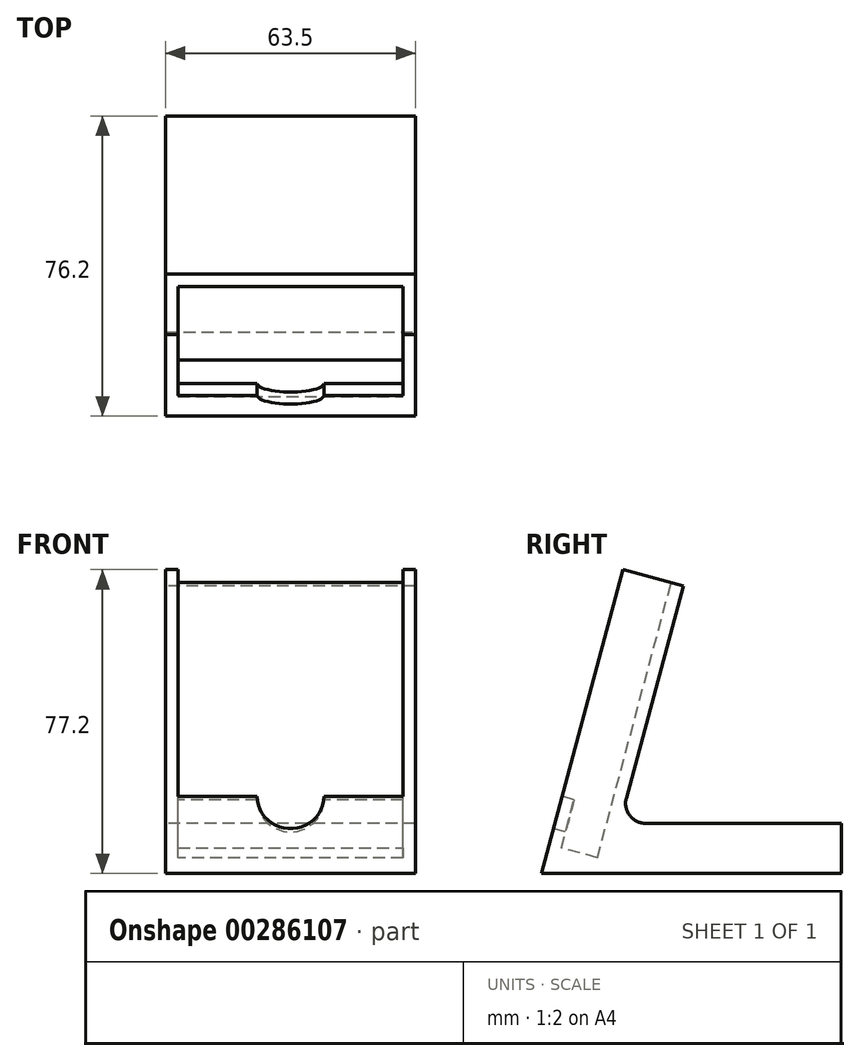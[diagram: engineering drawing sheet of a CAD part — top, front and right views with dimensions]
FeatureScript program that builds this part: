
annotation { "Feature Type Name" : "Feature", "Feature Type Description" : "" }
export const myFeature = defineFeature(function(context is Context, id is Id, definition is map)
    precondition{}
    {
        {
            var Q0;
            Q0=qCreatedBy(makeId("Right.planeOp"),FACE);
            var sketch = newSketch(context, id + "F0", { "sketchPlane" : qUnion([Q0])});
            skLineSegment(sketch, "E0", {"start": v(0, 0) * mm, "end": v(76.2, 0) * mm});
            skLineSegment(sketch, "E1", {"start": v(76.2, 0) * mm, "end": v(76.2, 12.7) * mm});
            skLineSegment(sketch, "E2", {"start": v(76.2, 12.7) * mm, "end": v(19.84, 12.7) * mm});
            skLineSegment(sketch, "E3", {"start": v(19.84, 12.7) * mm, "end": v(36.02, 73.09) * mm});
            skLineSegment(sketch, "E4", {"start": v(36.02, 73.09) * mm, "end": v(20.69, 77.2) * mm});
            skLineSegment(sketch, "E5", {"start": v(20.69, 77.2) * mm, "end": v(0, 0) * mm});
            skSolve(sketch);
        }
        {
            var Q0;
            Q0=makeQuery(id+"F0.imprint","IMPRINT",FACE,{"disambiguationData":[TD([[makeQuery(id+"F0.imprint","IMPRINT",EDGE,{"derivedFrom":sQuery(id+"F0.wireOp",EDGE,"E0")}),1.0]])]});
            extrude(context, id + "F1", {"entities" : qUnion([Q0]), "depth" : 63.5 * mm});
        }
        {
            var Q0;
            Q0=makeQuery(id+"F1.opExtrude","SWEPT_FACE",FACE,{"disambiguationData":[OSD([sQuery(id+"F0.wireOp",EDGE,"E4")])]});
            var sketch = newSketch(context, id + "F2", { "sketchPlane" : qUnion([Q0])});
            skLineSegment(sketch, "E6.0", {"start": v(3.18, 12.7) * mm, "end": v(3.18, 3.18) * mm});
            skLineSegment(sketch, "E6.1", {"start": v(60.33, 12.7) * mm, "end": v(3.17, 12.7) * mm});
            skLineSegment(sketch, "E6.2", {"start": v(60.33, 3.18) * mm, "end": v(60.33, 12.7) * mm});
            skLineSegment(sketch, "E6.3", {"start": v(3.17, 3.18) * mm, "end": v(60.33, 3.18) * mm});
            skSolve(sketch);
        }
        {
            var Q0;
            Q0=makeQuery(id+"F2.imprint","IMPRINT",FACE,{"disambiguationData":[TD([[makeQuery(id+"F2.imprint","IMPRINT",EDGE,{"derivedFrom":sQuery(id+"F2.wireOp",EDGE,"E6.0")}),1.0]])]});
            extrude(context, id + "F3", {"entities" : qUnion([Q0]), "operationType" : NewBodyOperationType.REMOVE, "oppositeDirection" : true, "depth" : 72.39 * mm});
        }
        {
            var Q0;
            Q0=makeQuery(id+"F1.opExtrude","SWEPT_FACE",FACE,{"disambiguationData":[OSD([sQuery(id+"F0.wireOp",EDGE,"E5")])]});
            var sketch = newSketch(context, id + "F4", { "sketchPlane" : qUnion([Q0])});
            skPoint(sketch, "E7.0", {"position": v(60.33, 79.92) * mm});
            skPoint(sketch, "E7.1", {"position": v(3.18, 79.92) * mm});
            skPoint(sketch, "E8.0", {"position": v(3.18, 7.53) * mm});
            skPoint(sketch, "E8.1", {"position": v(60.33, 7.53) * mm});
            skLineSegment(sketch, "E9.bottom", {"start": v(3.18, 79.92) * mm, "end": v(60.33, 79.92) * mm});
            skLineSegment(sketch, "E9.top", {"start": v(3.18, 20.23) * mm, "end": v(60.33, 20.23) * mm});
            skLineSegment(sketch, "E9.left", {"start": v(3.18, 79.92) * mm, "end": v(3.18, 20.23) * mm});
            skLineSegment(sketch, "E9.right", {"start": v(60.33, 79.92) * mm, "end": v(60.33, 20.23) * mm});
            skLineSegment(sketch, "E10", {"start": v(31.75, 20.23) * mm, "end": v(31.75, 7.53) * mm, "construction": true});
            skArc(sketch, "E11", {"start": v(40.22, 20.23) * mm, "mid": v(31.75, 28.7) * mm, "end": v(23.28, 20.23) * mm, "construction": true});
            skArc(sketch, "E12", {"start": v(23.28, 20.23) * mm, "mid": v(31.75, 11.76) * mm, "end": v(40.22, 20.23) * mm});
            skSolve(sketch);
        }
        {
            var Q0;
            Q0=makeQuery(id+"F4.imprint","IMPRINT",FACE,{"disambiguationData":[TD([[makeQuery(id+"F4.imprint","IMPRINT",EDGE,{"derivedFrom":sQuery(id+"F4.wireOp",EDGE,"E9.bottom")}),1.0]])]});
            var Q1;
            {var subQ0=sQuery(id+"F4.wireOp",EDGE,"E12");Q1=makeQuery(id+"F4.imprint","IMPRINT",FACE,{"disambiguationData":[TD([[makeQuery(id+"F4.imprint","IMPRINT",EDGE,{"derivedFrom":subQ0}),1.0]])]});}
            extrude(context, id + "F5", {"entities" : qUnion([Q0, Q1]), "operationType" : NewBodyOperationType.REMOVE, "endBound" : BoundingType.UP_TO_NEXT, "oppositeDirection" : true, "depth" : 25.4 * mm});
        }
        {
            var Q0;
            Q0=makeQuery(id+"F1.opExtrude","SWEPT_EDGE",EDGE,{"disambiguationData":[OSD([sQuery(id+"F0.wireOp",EDGE,"E2"),sQuery(id+"F0.wireOp",EDGE,"E3")])]});
            fillet(context, id + "F6", {"entities" : qUnion([Q0]), "radius" : 5.08 * mm, "tangentPropagation" : true, "allowEdgeOverflow" : false});
        }
    });
